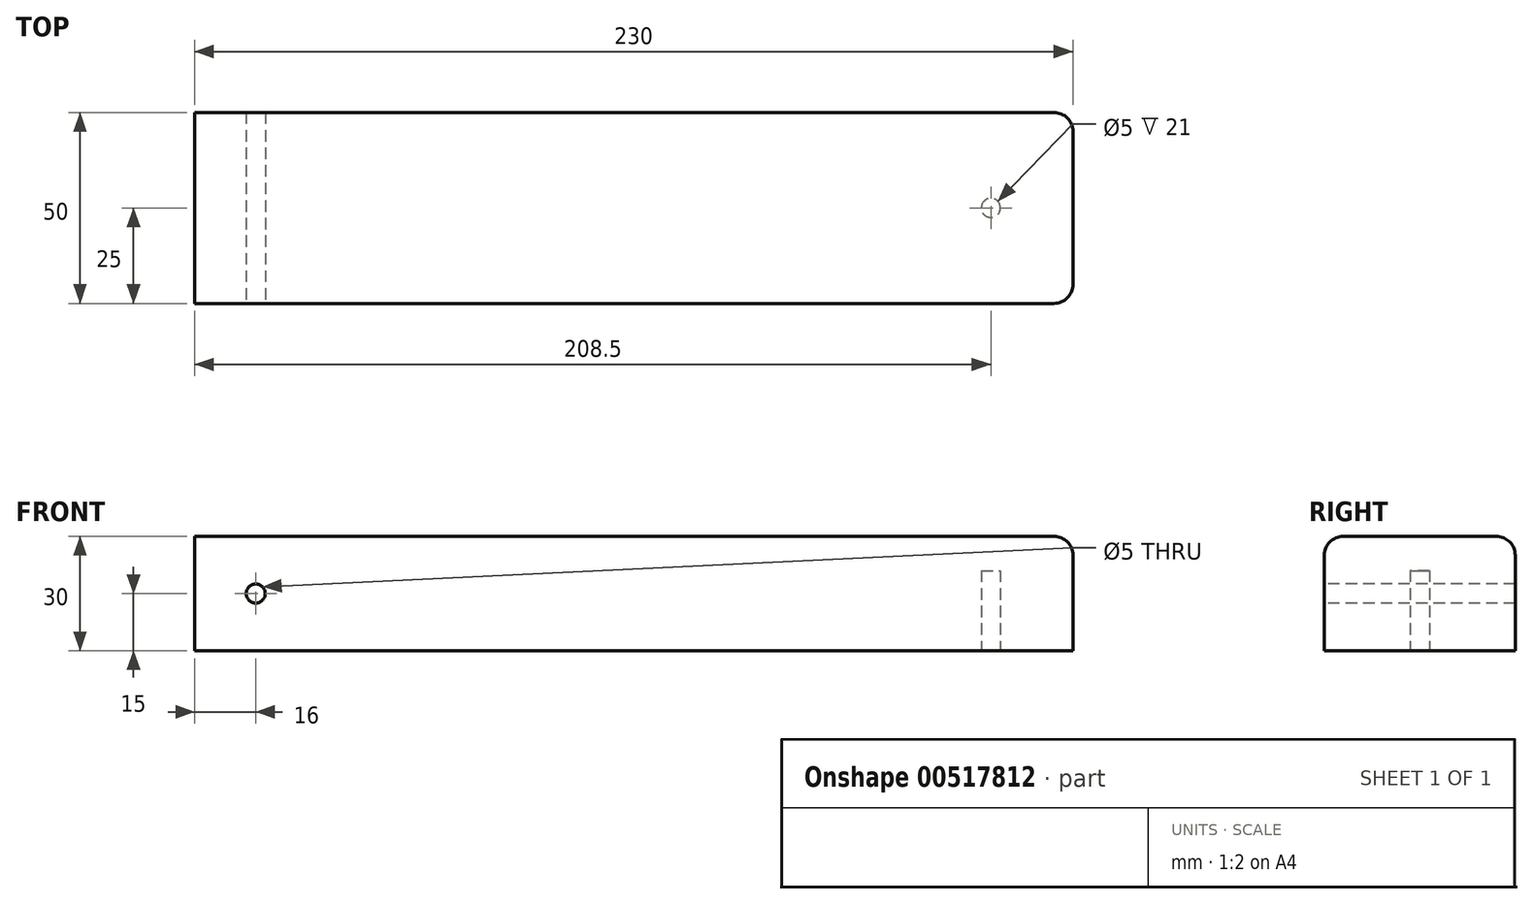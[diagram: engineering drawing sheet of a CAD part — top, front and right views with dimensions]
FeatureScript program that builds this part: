
annotation { "Feature Type Name" : "Feature", "Feature Type Description" : "" }
export const myFeature = defineFeature(function(context is Context, id is Id, definition is map)
    precondition{}
    {
        {
            var Q0;
            Q0=qCreatedBy(makeId("Top.planeOp"),FACE);
            var sketch = newSketch(context, id + "F0", { "sketchPlane" : qUnion([Q0])});
            skLineSegment(sketch, "E0.bottom", {"start": v(115, 25) * mm, "end": v(-115, 25) * mm});
            skLineSegment(sketch, "E0.top", {"start": v(115, -25) * mm, "end": v(-115, -25) * mm});
            skLineSegment(sketch, "E0.left", {"start": v(115, 25) * mm, "end": v(115, -25) * mm});
            skLineSegment(sketch, "E0.right", {"start": v(-115, 25) * mm, "end": v(-115, -25) * mm});
            skPoint(sketch, "E0.middle", {"position": v(0, 0) * mm});
            skSolve(sketch);
        }
        {
            var Q0;
            Q0=makeQuery(id+"F0.imprint","IMPRINT",FACE,{"disambiguationData":[TD([[makeQuery(id+"F0.imprint","IMPRINT",EDGE,{"derivedFrom":sQuery(id+"F0.wireOp",EDGE,"E0.bottom")}),1.0]])]});
            extrude(context, id + "F1", {"entities" : qUnion([Q0]), "depth" : 30 * mm, "offsetDistance" : 25 * mm});
        }
        {
            var Q0;
            Q0=makeQuery(id+"F1.opExtrude","SWEPT_EDGE",EDGE,{"disambiguationData":[OSD([sQuery(id+"F0.wireOp",EDGE,"E0.top"),sQuery(id+"F0.wireOp",EDGE,"E0.left")])]});
            var Q1;
            Q1=makeQuery(id+"F1.opExtrude","SWEPT_EDGE",EDGE,{"disambiguationData":[OSD([sQuery(id+"F0.wireOp",EDGE,"E0.bottom"),sQuery(id+"F0.wireOp",EDGE,"E0.left")])]});
            var Q2;
            Q2=makeQuery(id+"F1.opExtrude","CAP_EDGE",EDGE,{"disambiguationData":[OSD([sQuery(id+"F0.wireOp",EDGE,"E0.left")])],"isStart":false});
            var Q3;
            Q3=makeQuery(id+"F1.opExtrude","CAP_EDGE",EDGE,{"disambiguationData":[OSD([sQuery(id+"F0.wireOp",EDGE,"E0.bottom")])],"isStart":false});
            var Q4;
            Q4=makeQuery(id+"F1.opExtrude","CAP_EDGE",EDGE,{"disambiguationData":[OSD([sQuery(id+"F0.wireOp",EDGE,"E0.top")])],"isStart":false});
            fillet(context, id + "F2", {"entities" : qUnion([Q0, Q1, Q2, Q3, Q4]), "radius" : 5 * mm, "tangentPropagation" : true, "allowEdgeOverflow" : false});
        }
        {
            var Q0;
            Q0=makeQuery(id+"F1.opExtrude","SWEPT_FACE",FACE,{"disambiguationData":[OSD([sQuery(id+"F0.wireOp",EDGE,"E0.top")])]});
            var sketch = newSketch(context, id + "F3", { "sketchPlane" : qUnion([Q0])});
            skLineSegment(sketch, "E1", {"start": v(-115, 0) * mm, "end": v(-115, 15) * mm});
            skLineSegment(sketch, "E2", {"start": v(-115, 15) * mm, "end": v(-99, 15) * mm});
            skCircle(sketch, "E3", {"center": v(-99, 15) * mm, "radius": 2.5 * mm});
            skSolve(sketch);
        }
        {
            var Q0;
            Q0=makeQuery(id+"F3.imprint","IMPRINT",FACE,{"disambiguationData":[TD([[makeQuery(id+"F3.imprint","IMPRINT",EDGE,{"derivedFrom":sQuery(id+"F3.wireOp",EDGE,"E3")}),1.0]])]});
            extrude(context, id + "F4", {"entities" : qUnion([Q0]), "operationType" : NewBodyOperationType.REMOVE, "oppositeDirection" : true, "depth" : 76.7 * mm, "offsetDistance" : 25 * mm});
        }
        {
            var Q0;
            Q0=makeQuery(id+"F1.opExtrude","CAP_FACE",FACE,{"disambiguationData":[OSD([sQuery(id+"F0.wireOp",EDGE,"E0.bottom"),sQuery(id+"F0.wireOp",EDGE,"E0.top"),sQuery(id+"F0.wireOp",EDGE,"E0.left"),sQuery(id+"F0.wireOp",EDGE,"E0.right")])],"isStart":true});
            var sketch = newSketch(context, id + "F5", { "sketchPlane" : qUnion([Q0])});
            skLineSegment(sketch, "E4", {"start": v(115, 0) * mm, "end": v(93.5, 0) * mm});
            skCircle(sketch, "E5", {"center": v(93.5, 0) * mm, "radius": 2.5 * mm});
            skSolve(sketch);
        }
        {
            var Q0;
            Q0=makeQuery(id+"F5.imprint","IMPRINT",FACE,{"disambiguationData":[TD([[makeQuery(id+"F5.imprint","IMPRINT",EDGE,{"derivedFrom":sQuery(id+"F5.wireOp",EDGE,"E5")}),1.0]])]});
            extrude(context, id + "F6", {"entities" : qUnion([Q0]), "operationType" : NewBodyOperationType.REMOVE, "oppositeDirection" : true, "depth" : 21 * mm, "offsetDistance" : 25 * mm});
        }
    });
